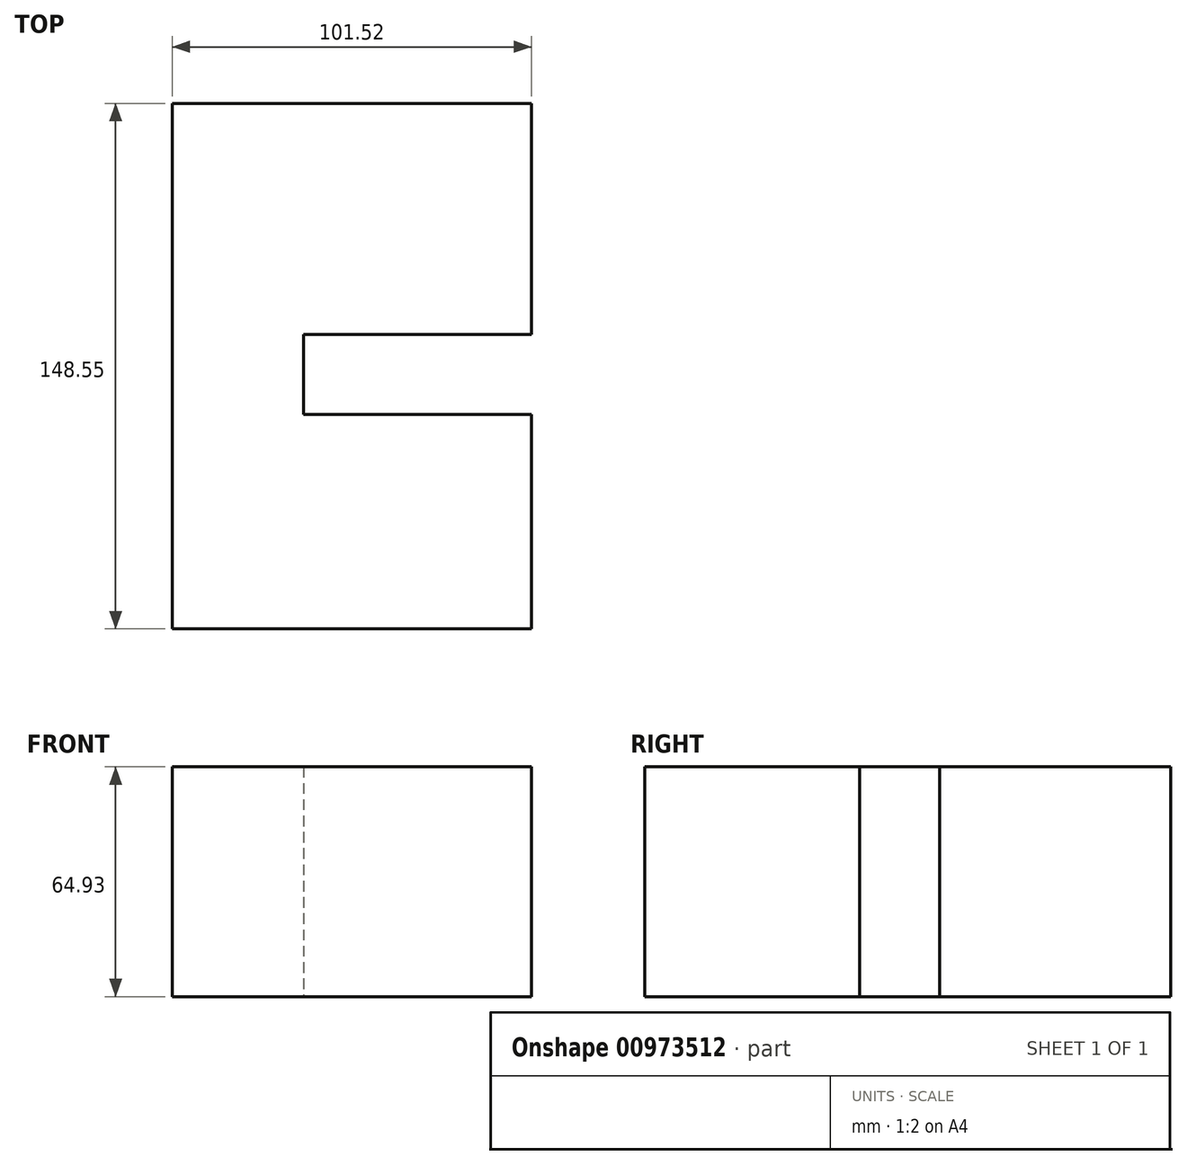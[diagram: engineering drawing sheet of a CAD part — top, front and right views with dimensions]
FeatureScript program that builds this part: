
annotation { "Feature Type Name" : "Feature", "Feature Type Description" : "" }
export const myFeature = defineFeature(function(context is Context, id is Id, definition is map)
    precondition{}
    {
        {
            var Q0;
            Q0=qCreatedBy(makeId("Top.planeOp"),FACE);
            var sketch = newSketch(context, id + "F0", { "sketchPlane" : qUnion([Q0])});
            skLineSegment(sketch, "E0.bottom", {"start": v(-37.04, 37.12) * mm, "end": v(64.48, 37.12) * mm});
            skLineSegment(sketch, "E0.top", {"start": v(-37.04, -28.2) * mm, "end": v(64.48, -28.2) * mm});
            skLineSegment(sketch, "E0.left", {"start": v(-37.04, 37.12) * mm, "end": v(-37.04, -28.2) * mm});
            skLineSegment(sketch, "E0.right", {"start": v(64.48, 37.12) * mm, "end": v(64.48, -28.2) * mm});
            skLineSegment(sketch, "E1.bottom", {"start": v(13.72, 37.12) * mm, "end": v(13.72, 37.12) * mm});
            skLineSegment(sketch, "E1.top", {"start": v(13.72, -28.2) * mm, "end": v(13.72, -28.2) * mm});
            skLineSegment(sketch, "E1.left", {"start": v(13.72, 37.12) * mm, "end": v(13.72, -28.2) * mm});
            skLineSegment(sketch, "E1.right", {"start": v(13.72, 37.12) * mm, "end": v(13.72, -28.2) * mm});
            skSolve(sketch);
        }
        {
            var Q0;
            {var subQ0=sQuery(id+"F0.wireOp",EDGE,"E0.left");Q0=makeQuery(id+"F0.imprint","IMPRINT",FACE,{"disambiguationData":[TD([[makeQuery(id+"F0.imprint","IMPRINT",EDGE,{"derivedFrom":subQ0}),1.0]])]});}
            var Q1;
            {var subQ0=sQuery(id+"F0.wireOp",EDGE,"E0.right");Q1=makeQuery(id+"F0.imprint","IMPRINT",FACE,{"disambiguationData":[TD([[makeQuery(id+"F0.imprint","IMPRINT",EDGE,{"derivedFrom":subQ0}),-1.0]])]});}
            extrude(context, id + "F1", {"entities" : qUnion([Q0, Q1]), "depth" : 64.93 * mm, "offsetDistance" : 25.4 * mm});
        }
        {
            var Q0;
            Q0=qCreatedBy(makeId("Front.planeOp"),FACE);
            cPlane(context, id + "F2", {"entities" : qUnion([Q0]), "cplaneType" : CPlaneType.OFFSET, "offset" : 50.8 * mm, "width" : 152.4 * mm, "height" : 152.4 * mm});
        }
        {
            var Q0;
            Q0=qCreatedBy(id+"F2.planeOp",FACE);
            var sketch = newSketch(context, id + "F3", { "sketchPlane" : qUnion([Q0])});
            skLineSegment(sketch, "E2.0.0", {"start": v(-37.04, 0) * mm, "end": v(64.48, 0) * mm});
            skLineSegment(sketch, "E2.0.1", {"start": v(64.48, 0) * mm, "end": v(64.48, 64.93) * mm});
            skLineSegment(sketch, "E2.0.2", {"start": v(64.48, 64.93) * mm, "end": v(-37.04, 64.93) * mm});
            skLineSegment(sketch, "E2.0.3", {"start": v(-37.04, 64.93) * mm, "end": v(-37.04, 0) * mm});
            skSolve(sketch);
        }
        {
            var Q0;
            Q0=makeQuery(id+"F3.imprint","IMPRINT",FACE,{"disambiguationData":[TD([[makeQuery(id+"F3.imprint","IMPRINT",EDGE,{"derivedFrom":sQuery(id+"F3.wireOp",EDGE,"E2.0.0")}),1.0]])]});
            extrude(context, id + "F4", {"entities" : qUnion([Q0]), "depth" : 60.63 * mm, "offsetDistance" : 25.4 * mm});
        }
        {
            var Q0;
            Q0=makeQuery(id+"F1.opExtrude","SWEPT_FACE",FACE,{"disambiguationData":[OSD([sQuery(id+"F0.wireOp",EDGE,"E0.top")])]});
            var sketch = newSketch(context, id + "F5", { "sketchPlane" : qUnion([Q0])});
            skLineSegment(sketch, "E3.bottom", {"start": v(-37.04, 64.93) * mm, "end": v(0, 64.93) * mm});
            skLineSegment(sketch, "E3.top", {"start": v(-37.04, 0) * mm, "end": v(0, 0) * mm});
            skLineSegment(sketch, "E3.left", {"start": v(-37.04, 64.93) * mm, "end": v(-37.04, 0) * mm});
            skLineSegment(sketch, "E3.right", {"start": v(0, 64.93) * mm, "end": v(0, 0) * mm});
            skSolve(sketch);
        }
        {
            var Q0;
            Q0=makeQuery(id+"F5.imprint","IMPRINT",FACE,{"disambiguationData":[TD([[makeQuery(id+"F5.imprint","IMPRINT",EDGE,{"derivedFrom":sQuery(id+"F5.wireOp",EDGE,"E3.bottom")}),-1.0]])]});
            var Q1;
            Q1=makeQuery(id+"F4.opExtrude","CAP_FACE",FACE,{"disambiguationData":[OSD([sQuery(id+"F3.wireOp",EDGE,"E2.0.0"),sQuery(id+"F3.wireOp",EDGE,"E2.0.1"),sQuery(id+"F3.wireOp",EDGE,"E2.0.2"),sQuery(id+"F3.wireOp",EDGE,"E2.0.3")])],"isStart":true});
            extrude(context, id + "F6", {"entities" : qUnion([Q0]), "endBound" : BoundingType.UP_TO_SURFACE, "depth" : 25.4 * mm, "endBoundEntityFace" : qUnion([Q1]), "offsetDistance" : 25.4 * mm});
        }
        {
            var Q0;
            Q0=makeQuery(id+"F1.opExtrude","SWEPT_BODY",BODY,{"disambiguationData":[OSD([sQuery(id+"F0.wireOp",EDGE,"E0.bottom"),sQuery(id+"F0.wireOp",EDGE,"E0.top"),sQuery(id+"F0.wireOp",EDGE,"E0.left"),sQuery(id+"F0.wireOp",EDGE,"E0.right")])]});
            var Q1;
            Q1=makeQuery(id+"F4.opExtrude","SWEPT_BODY",BODY,{"disambiguationData":[OSD([sQuery(id+"F3.wireOp",EDGE,"E2.0.0"),sQuery(id+"F3.wireOp",EDGE,"E2.0.1"),sQuery(id+"F3.wireOp",EDGE,"E2.0.2"),sQuery(id+"F3.wireOp",EDGE,"E2.0.3")])]});
            var Q2;
            Q2=makeQuery(id+"F6.opExtrude","SWEPT_BODY",BODY,{"disambiguationData":[OSD([sQuery(id+"F5.wireOp",EDGE,"E3.bottom"),sQuery(id+"F5.wireOp",EDGE,"E3.top"),sQuery(id+"F5.wireOp",EDGE,"E3.left"),sQuery(id+"F5.wireOp",EDGE,"E3.right")])]});
            booleanBodies(context, id + "F7", {"operationType" : BooleanOperationType.UNION, "tools" : qUnion([Q0, Q1, Q2])});
        }
    });
